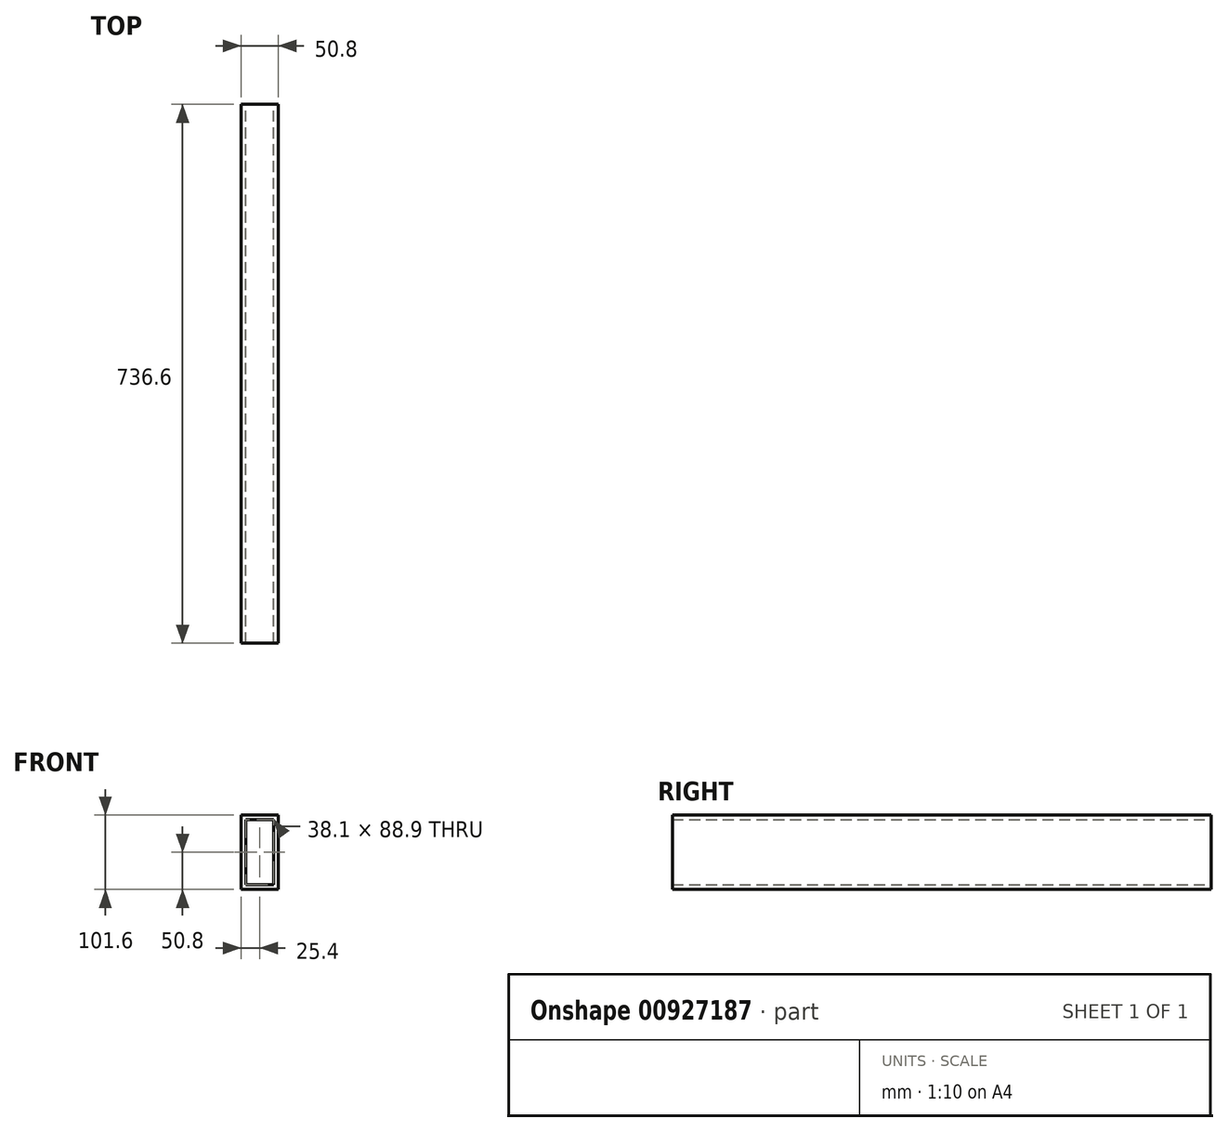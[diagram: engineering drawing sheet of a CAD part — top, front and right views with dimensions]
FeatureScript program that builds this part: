
annotation { "Feature Type Name" : "Feature", "Feature Type Description" : "" }
export const myFeature = defineFeature(function(context is Context, id is Id, definition is map)
    precondition{}
    {
        {
            var Q0;
            Q0=qCreatedBy(makeId("Front.planeOp"),FACE);
            var sketch = newSketch(context, id + "F0", { "sketchPlane" : qUnion([Q0])});
            skLineSegment(sketch, "E0.bottom", {"start": v(25.4, 50.8) * mm, "end": v(-25.4, 50.8) * mm});
            skLineSegment(sketch, "E0.top", {"start": v(25.4, -50.8) * mm, "end": v(-25.4, -50.8) * mm});
            skLineSegment(sketch, "E0.left", {"start": v(25.4, 50.8) * mm, "end": v(25.4, -50.8) * mm});
            skLineSegment(sketch, "E0.right", {"start": v(-25.4, 50.8) * mm, "end": v(-25.4, -50.8) * mm});
            skPoint(sketch, "E0.middle", {"position": v(0, 0) * mm});
            skLineSegment(sketch, "E1.0", {"start": v(19.05, 44.45) * mm, "end": v(-19.05, 44.45) * mm});
            skLineSegment(sketch, "E1.1", {"start": v(19.05, 44.45) * mm, "end": v(19.05, -44.45) * mm});
            skLineSegment(sketch, "E1.2", {"start": v(19.05, -44.45) * mm, "end": v(-19.05, -44.45) * mm});
            skLineSegment(sketch, "E1.3", {"start": v(-19.05, 44.45) * mm, "end": v(-19.05, -44.45) * mm});
            skSolve(sketch);
        }
        {
            var Q0;
            Q0 = qSketchRegion(id + "F0", true);
            extrude(context, id + "F1", {"entities" : qUnion([Q0]), "endBound" : BoundingType.SYMMETRIC, "depth" : 736.6 * mm, "offsetDistance" : 25.4 * mm});
        }
    });
